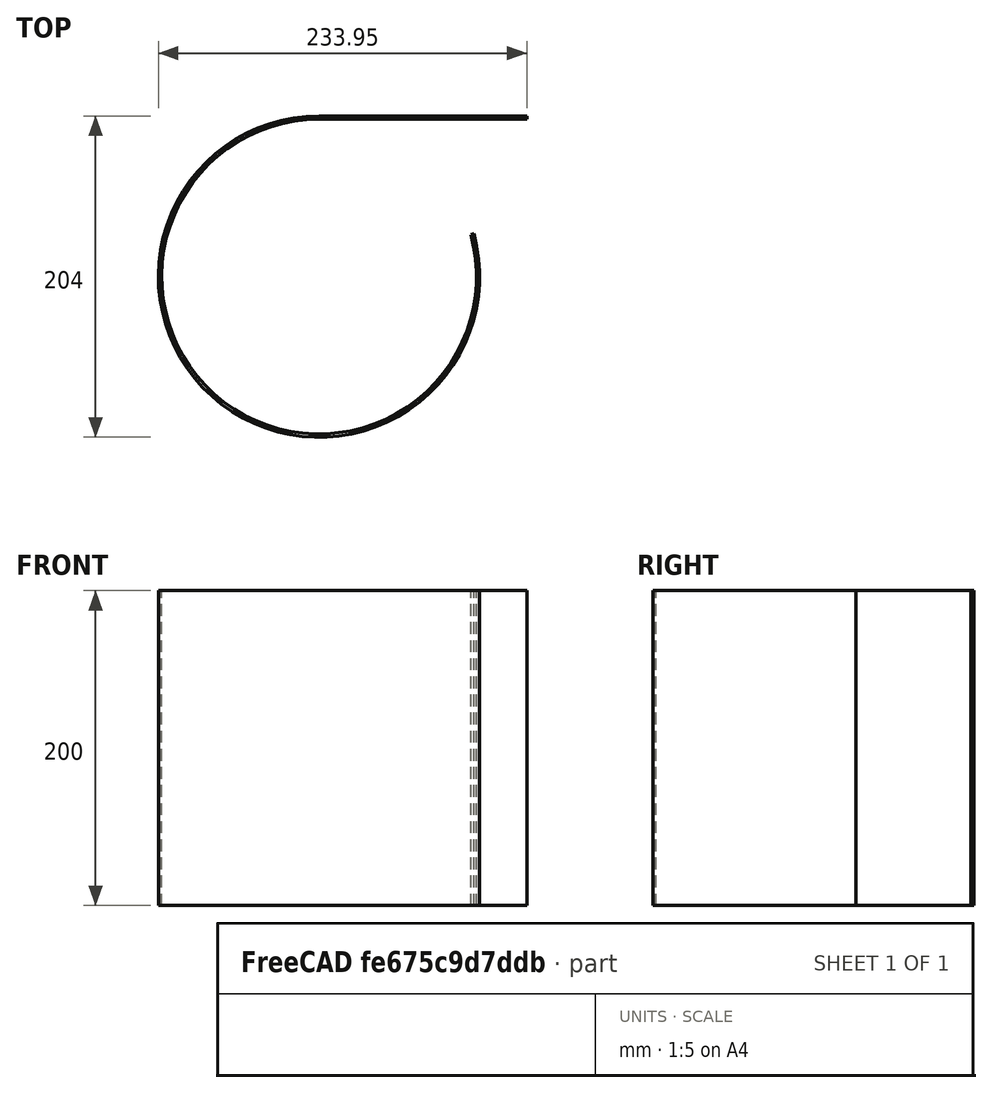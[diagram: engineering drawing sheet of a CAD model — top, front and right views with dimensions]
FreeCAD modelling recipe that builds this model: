
FCSTD DOCUMENT  (FreeCAD 0.18.2R)
Label: 212 - ROLL A SHEET
License: All rights reserved
LicenseURL: http://en.wikipedia.org/wiki/All_rights_reserved
objects: Sketcher::SketchObject×1, PartDesign::Body×1, Part::Plane×1, Part::Sweep×1, App::DocumentObjectGroupPython×1, Spreadsheet::Sheet×1
note: 4 computed .brp shape members not serialized (recipe doc carries the construction recipe); baked Part::Feature solids carry a one-line shape summary decoded from their .brp

FEATURE [Sketcher::SketchObject] Sketch
  MapMode = 5
  Support = -> [XY_Plane]
  expr: Constraints[5] = Spreadsheet.ang
  expr: Constraints[7] = Spreadsheet.l1
  expr: Constraints[6] = Spreadsheet.r1
  sketch-geometry (3):
    g0: LineSegment StartX=131.947 StartY=0 StartZ=0 EndX=0 EndY=0 EndZ=0
    g1: ArcOfCircle CenterX=0 CenterY=-100 CenterZ=0 NormalX=0 NormalY=0 NormalZ=1 AngleXU=0 Radius=100 StartAngle=1.5708 EndAngle=6.55284
    g2: LineSegment [constr] StartX=96.3863 StartY=-73.3603 StartZ=0 EndX=0 EndY=-100 EndZ=0
  constraints (8):
    c: PointOnObject(g0,g-1)
    c: Coincident(g0,g-1)
    c: Tangent(g0,g1) = -1.5708
    c: Coincident(g2,g1)
    c: Coincident(g2,g1)
    c: Angle(g2,g-2) = 1.30114
    c: Radius(g1) = 100
    c: Distance(g0) = 131.947
FEATURE [PartDesign::Body] Body
  Group = -> [Sketch]
  Origin = -> Origin
FEATURE [Part::Plane] Plane
  AttacherType = Attacher::AttachEngine3D
  Length = 200
  Placement = pos=(0,0,0) rot=(0,1,0;4.71239rad)
  Width = 2
FEATURE [Part::Sweep] Sweep
  Frenet = true
  Sections = -> [Plane]
  Solid = true
  Spine = -> Sketch
  Transition = 1
FEATURE [App::DocumentObjectGroupPython] My_Manager  # scripted group (container) (typed FeaturePython)
  intervall = 100
  sleeptime = 0.02
  start = 0
  step = 21
  text = NO
FEATURE [Spreadsheet::Sheet] Spreadsheet
  cells = A1=angle=; B1(ang)==My_Manager.step * 3.55; A2=r1=; B2(r1)=100; A3=l1=; B3(l1)==2 * pi * B2 * B1 / 355
